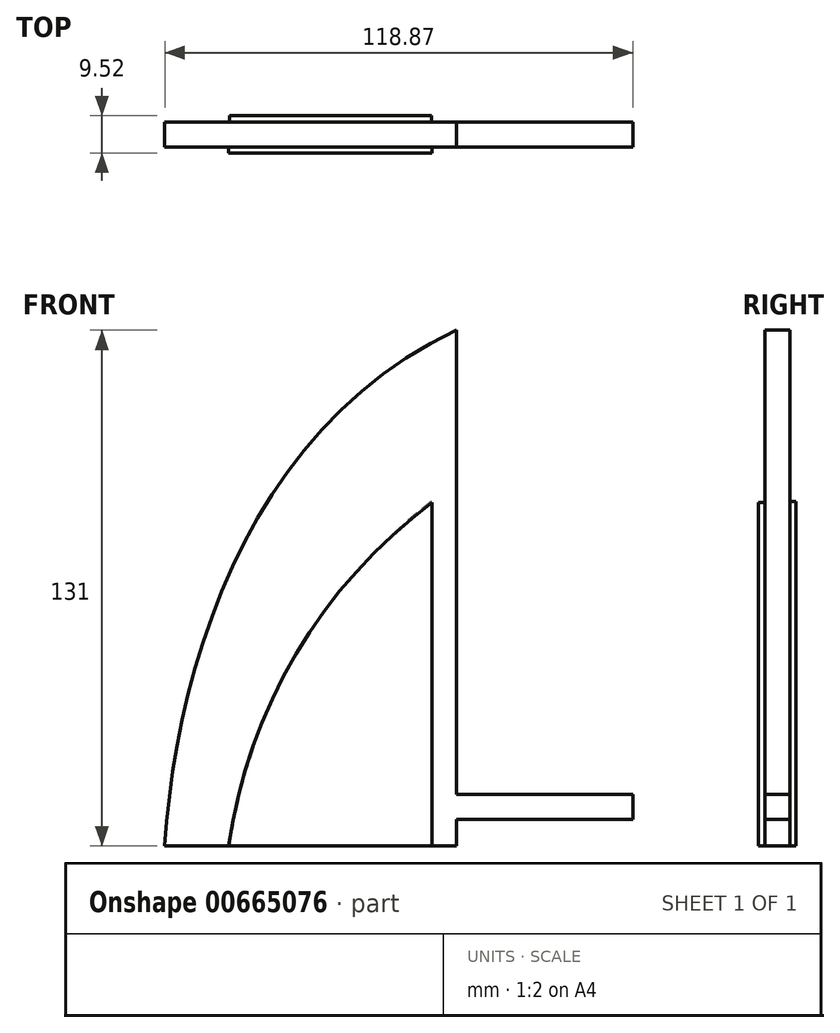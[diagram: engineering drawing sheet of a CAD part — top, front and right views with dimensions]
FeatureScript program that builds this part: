
annotation { "Feature Type Name" : "Feature", "Feature Type Description" : "" }
export const myFeature = defineFeature(function(context is Context, id is Id, definition is map)
    precondition{}
    {
        {
            var Q0;
            Q0=qCreatedBy(makeId("Front.planeOp"),FACE);
            var sketch = newSketch(context, id + "F0", { "sketchPlane" : qUnion([Q0])});
            skLineSegment(sketch, "E0", {"start": v(-63.58, -61.16) * mm, "end": v(10.53, -61.16) * mm});
            skLineSegment(sketch, "E1", {"start": v(10.53, -61.16) * mm, "end": v(10.53, 69.84) * mm});
            skFitSpline(sketch, "E2", {"points": [v(-63.58, -61.16) * mm, v(10.53, 69.84) * mm], "startDerivative": vector(8.94, 140.94) * mm, "endDerivative": vector(155.63, 71.9) * mm});
            skLineSegment(sketch, "E3.bottom", {"start": v(6.6, -48.09) * mm, "end": v(55.29, -48.09) * mm});
            skLineSegment(sketch, "E3.top", {"start": v(6.6, -54.44) * mm, "end": v(55.29, -54.44) * mm});
            skLineSegment(sketch, "E3.left", {"start": v(6.6, -48.09) * mm, "end": v(6.6, -54.44) * mm});
            skLineSegment(sketch, "E3.right", {"start": v(55.29, -48.09) * mm, "end": v(55.29, -54.44) * mm});
            skLineSegment(sketch, "E4", {"start": v(49.14, -48.09) * mm, "end": v(49.14, -54.44) * mm});
            skSolve(sketch);
        }
        {
            var Q0;
            Q0 = qSketchRegion(id + "F0", true);
            extrude(context, id + "F1", {"entities" : qUnion([Q0]), "endBound" : BoundingType.SYMMETRIC, "depth" : 6.35 * mm, "offsetDistance" : 25.4 * mm});
        }
        {
            var Q0;
            Q0=makeQuery(id+"F1.opExtrude","CAP_FACE",FACE,{"disambiguationData":[OSD([sQuery(id+"F0.wireOp",EDGE,"E0"),sQuery(id+"F0.wireOp",EDGE,"E1"),sQuery(id+"F0.wireOp",EDGE,"E2"),sQuery(id+"F0.wireOp",EDGE,"E3.bottom"),sQuery(id+"F0.wireOp",EDGE,"E3.top"),sQuery(id+"F0.wireOp",EDGE,"E3.right")])],"isStart":true});
            var sketch = newSketch(context, id + "F2", { "sketchPlane" : qUnion([Q0])});
            skLineSegment(sketch, "E5", {"start": v(-4.12, -61.16) * mm, "end": v(-4.12, 26.3) * mm});
            skArc(sketch, "E6", {"start": v(47.15, -61.16) * mm, "mid": v(30.1, -12.4) * mm, "end": v(-4.12, 26.3) * mm});
            skLineSegment(sketch, "E7", {"start": v(-4.12, -61.16) * mm, "end": v(47.15, -61.16) * mm});
            skSolve(sketch);
        }
        {
            var Q0;
            Q0=makeQuery(id+"F2.imprint","IMPRINT",FACE,{"disambiguationData":[TD([[makeQuery(id+"F2.imprint","IMPRINT",EDGE,{"derivedFrom":sQuery(id+"F2.wireOp",EDGE,"E5")}),-1.0]])]});
            extrude(context, id + "F3", {"entities" : qUnion([Q0]), "operationType" : NewBodyOperationType.ADD, "endBound" : BoundingType.SYMMETRIC, "depth" : 3.17 * mm, "offsetDistance" : 25.4 * mm});
        }
        {
            var Q0;
            Q0=makeQuery(id+"F1.opExtrude","CAP_FACE",FACE,{"disambiguationData":[OSD([sQuery(id+"F0.wireOp",EDGE,"E0"),sQuery(id+"F0.wireOp",EDGE,"E1"),sQuery(id+"F0.wireOp",EDGE,"E2"),sQuery(id+"F0.wireOp",EDGE,"E3.bottom"),sQuery(id+"F0.wireOp",EDGE,"E3.top"),sQuery(id+"F0.wireOp",EDGE,"E3.right")])],"isStart":false});
            var sketch = newSketch(context, id + "F4", { "sketchPlane" : qUnion([Q0])});
            skLineSegment(sketch, "E8", {"start": v(4.35, -61.16) * mm, "end": v(4.35, 26.08) * mm});
            skLineSegment(sketch, "E9", {"start": v(-47.4, -61.16) * mm, "end": v(4.35, -61.16) * mm});
            skArc(sketch, "E10", {"start": v(4.35, 26.08) * mm, "mid": v(-30.23, -12.38) * mm, "end": v(-47.4, -61.16) * mm});
            skSolve(sketch);
        }
        {
            var Q0;
            Q0 = qSketchRegion(id + "F4", true);
            extrude(context, id + "F5", {"entities" : qUnion([Q0]), "operationType" : NewBodyOperationType.ADD, "endBound" : BoundingType.SYMMETRIC, "depth" : 3.17 * mm, "offsetDistance" : 25.4 * mm});
        }
    });
